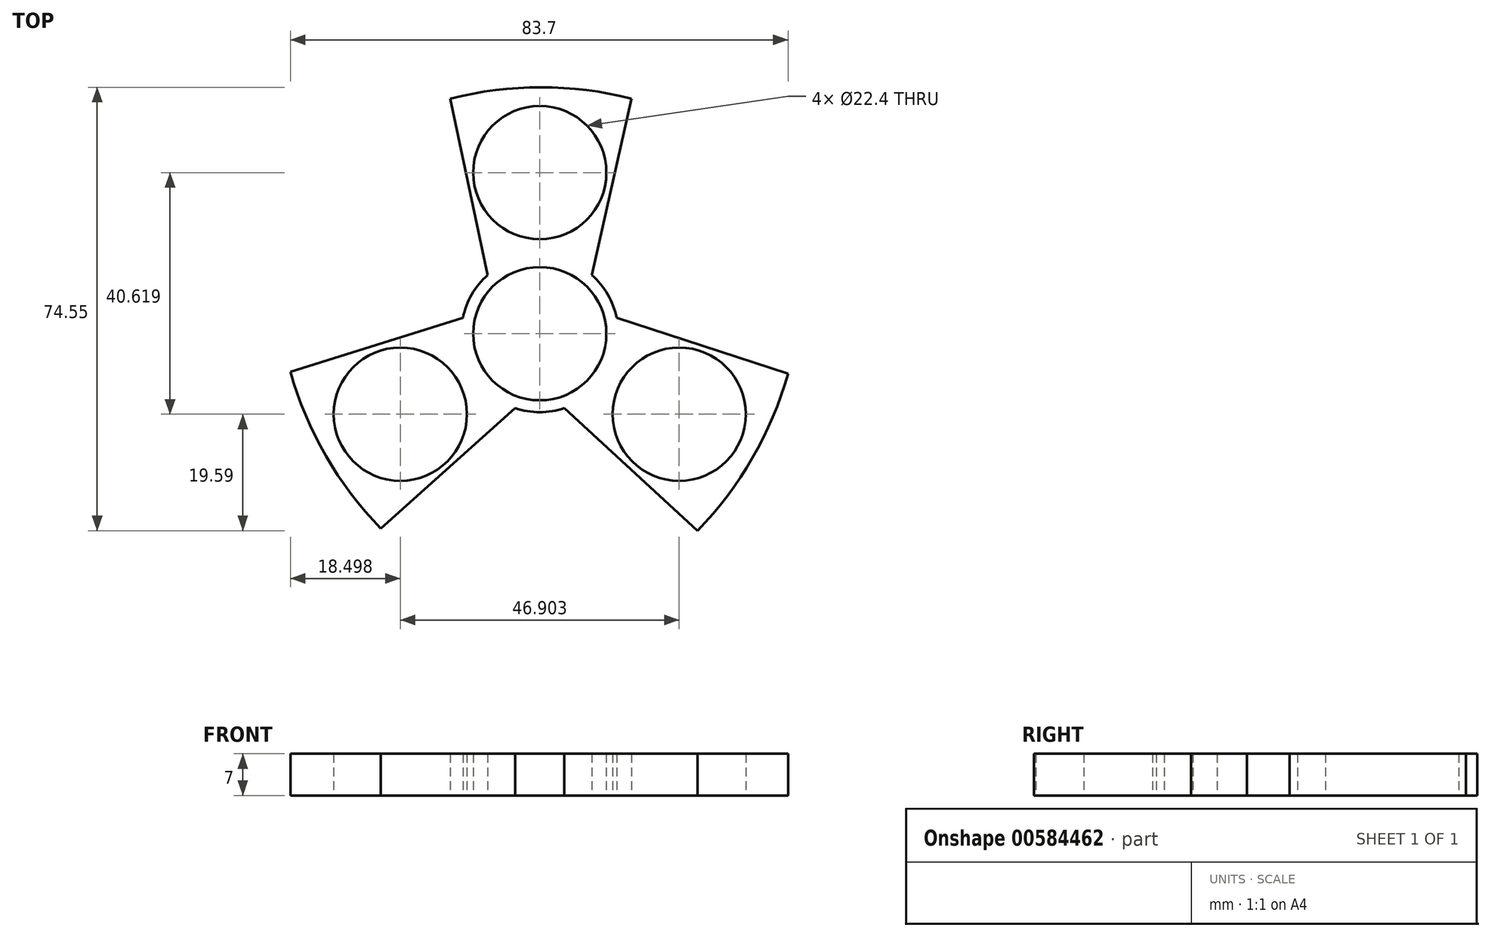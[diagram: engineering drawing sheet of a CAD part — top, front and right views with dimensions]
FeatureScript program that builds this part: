
annotation { "Feature Type Name" : "Feature", "Feature Type Description" : "" }
export const myFeature = defineFeature(function(context is Context, id is Id, definition is map)
    precondition{}
    {
        {
            var Q0;
            Q0=qCreatedBy(makeId("Top.planeOp"),FACE);
            var sketch = newSketch(context, id + "F0", { "sketchPlane" : qUnion([Q0])});
            skCircle(sketch, "E0", {"center": v(0, 0) * mm, "radius": 11.2 * mm});
            skCircle(sketch, "E1", {"center": v(0, 0) * mm, "radius": 13.2 * mm});
            skCircle(sketch, "E2", {"center": v(0, 27.08) * mm, "radius": 11.2 * mm});
            skPoint(sketch, "E3.center", {"position": v(17.35, -0.3) * mm});
            skLineSegment(sketch, "E4", {"start": v(-8.78, 9.85) * mm, "end": v(-15.03, 39.52) * mm});
            skLineSegment(sketch, "E5", {"start": v(8.78, 9.85) * mm, "end": v(15.43, 39.52) * mm});
            skArc(sketch, "E6", {"start": v(15.43, 39.52) * mm, "mid": v(0.2, 41.42) * mm, "end": v(-15.03, 39.52) * mm});
            skArc(sketch, "E7.1.0", {"start": v(-41.95, -6.4) * mm, "mid": v(-35.97, -20.54) * mm, "end": v(-26.71, -32.78) * mm});
            skLineSegment(sketch, "E7.1.1", {"start": v(-12.93, 2.68) * mm, "end": v(-41.95, -6.4) * mm});
            skCircle(sketch, "E7.1.2", {"center": v(-23.45, -13.54) * mm, "radius": 11.2 * mm});
            skLineSegment(sketch, "E7.1.3", {"start": v(-4.14, -12.53) * mm, "end": v(-26.71, -32.78) * mm});
            skArc(sketch, "E7.2.0", {"start": v(26.51, -33.13) * mm, "mid": v(35.77, -20.88) * mm, "end": v(41.75, -6.74) * mm});
            skLineSegment(sketch, "E7.2.1", {"start": v(4.14, -12.53) * mm, "end": v(26.51, -33.13) * mm});
            skCircle(sketch, "E7.2.2", {"center": v(23.45, -13.54) * mm, "radius": 11.2 * mm});
            skLineSegment(sketch, "E7.2.3", {"start": v(12.93, 2.68) * mm, "end": v(41.75, -6.74) * mm});
            skSolve(sketch);
        }
        {
            var Q0;
            Q0 = qSketchRegion(id + "F0", true);
            extrude(context, id + "F1", {"entities" : qUnion([Q0]), "depth" : 7 * mm, "offsetDistance" : 25 * mm});
        }
    });
